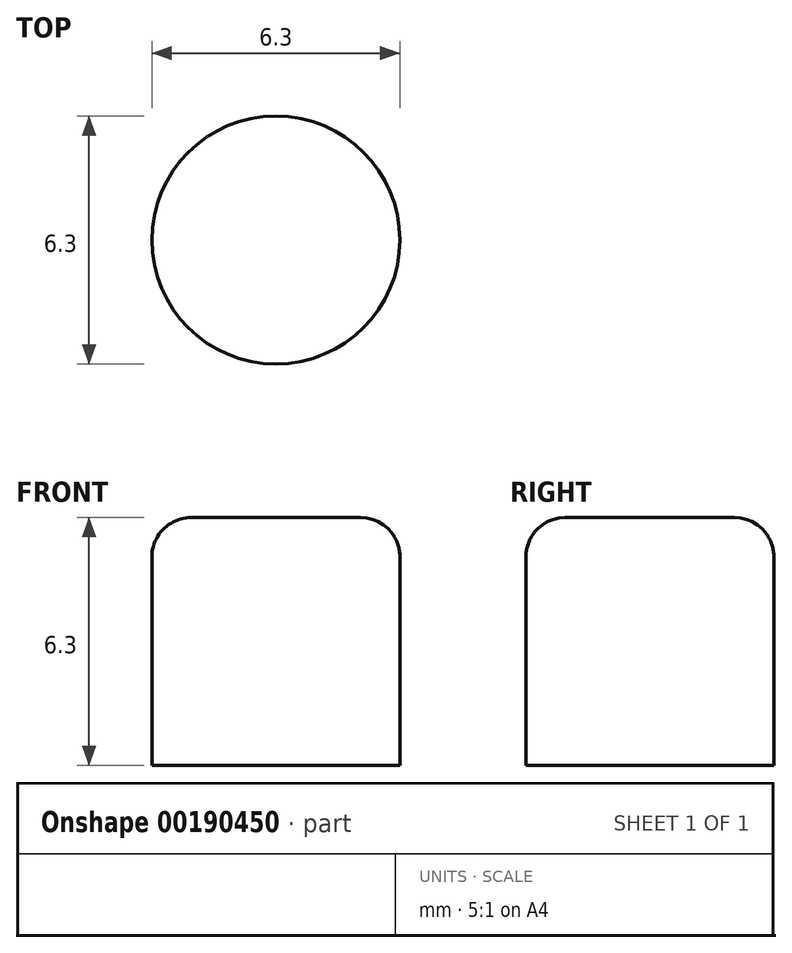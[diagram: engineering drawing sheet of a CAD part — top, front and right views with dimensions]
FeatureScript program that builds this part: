
annotation { "Feature Type Name" : "Feature", "Feature Type Description" : "" }
export const myFeature = defineFeature(function(context is Context, id is Id, definition is map)
    precondition{}
    {
        {
            var Q0;
            Q0=qCreatedBy(makeId("Right.planeOp"),FACE);
            var sketch = newSketch(context, id + "F0", { "sketchPlane" : qUnion([Q0])});
            skLineSegment(sketch, "E0", {"start": v(0, 0) * mm, "end": v(0, 6.3) * mm});
            skLineSegment(sketch, "E1", {"start": v(0, 6.3) * mm, "end": v(2.15, 6.3) * mm});
            skLineSegment(sketch, "E2", {"start": v(3.15, 5.3) * mm, "end": v(3.15, 0) * mm});
            skLineSegment(sketch, "E3", {"start": v(3.15, 0) * mm, "end": v(0, 0) * mm});
            skPoint(sketch, "E4.visualSharp", {"position": v(3.15, 6.3) * mm});
            skArc(sketch, "E4.filletArc", {"start": v(3.15, 5.3) * mm, "mid": v(2.86, 6) * mm, "end": v(2.15, 6.3) * mm});
            skSolve(sketch);
        }
        {
            var Q0;
            Q0=qSketchRegion(id+"F0",true);
            var Q1;
            Q1=sQuery(id+"F0.wireOp",EDGE,"E0");
            revolve(context, id + "F1", {"entities" : qUnion([Q0]), "axis" : qUnion([Q1]), "revolveType" : RevolveType.FULL});
        }
    });
